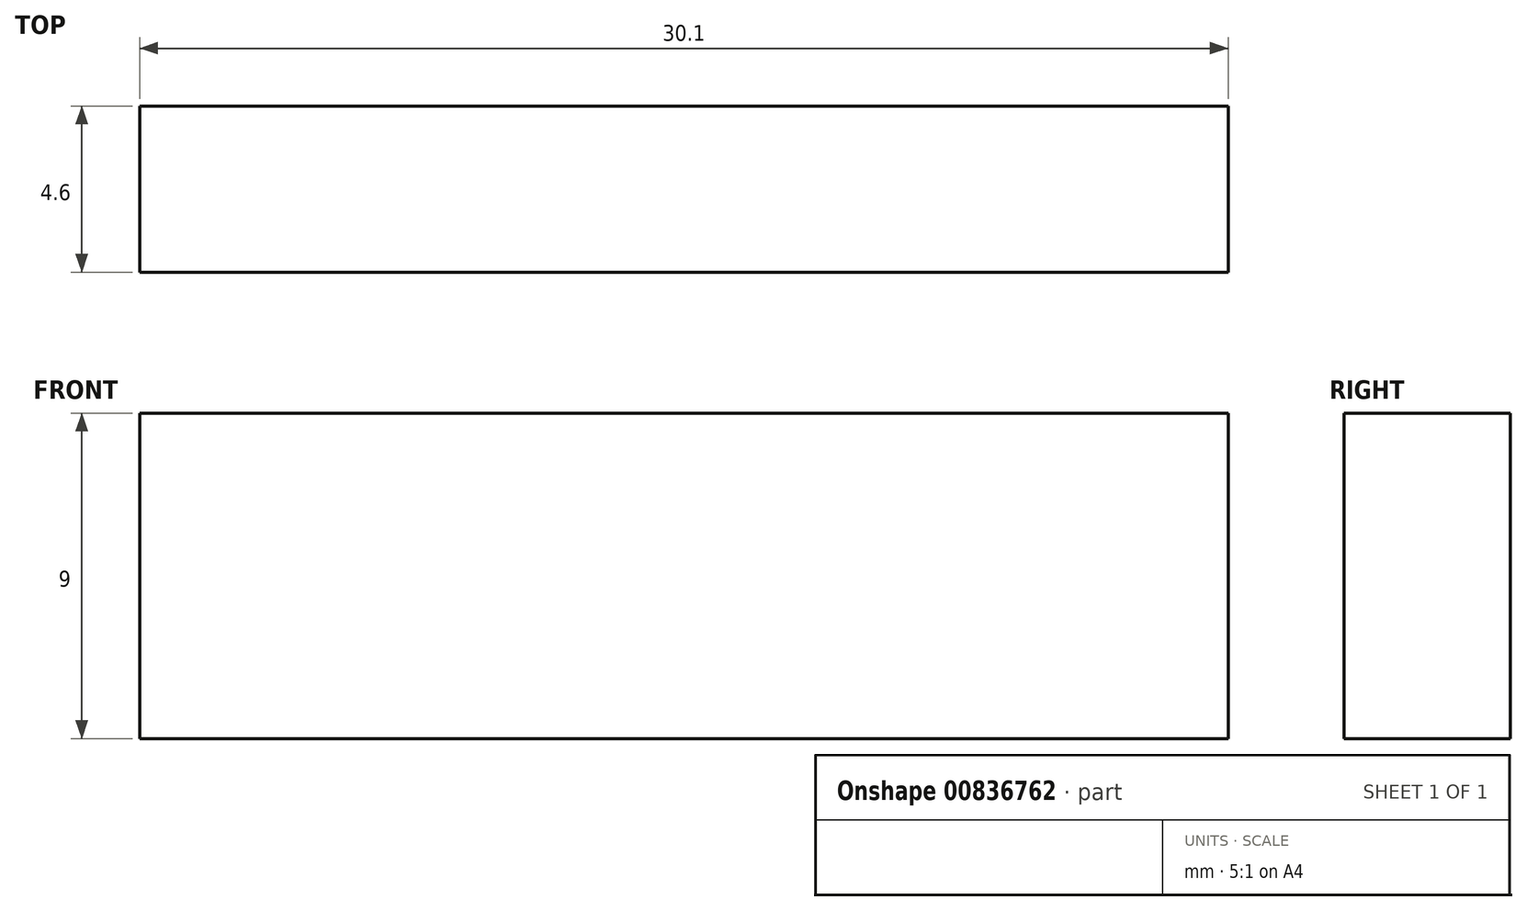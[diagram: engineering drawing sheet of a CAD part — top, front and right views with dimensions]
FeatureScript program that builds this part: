
annotation { "Feature Type Name" : "Feature", "Feature Type Description" : "" }
export const myFeature = defineFeature(function(context is Context, id is Id, definition is map)
    precondition{}
    {
        {
            var Q0;
            Q0=qCreatedBy(makeId("Top.planeOp"),FACE);
            var sketch = newSketch(context, id + "F0", { "sketchPlane" : qUnion([Q0])});
            skLineSegment(sketch, "E0.bottom", {"start": v(15.05, 2.3) * mm, "end": v(-15.05, 2.3) * mm});
            skLineSegment(sketch, "E0.top", {"start": v(15.05, -2.3) * mm, "end": v(-15.05, -2.3) * mm});
            skLineSegment(sketch, "E0.left", {"start": v(15.05, 2.3) * mm, "end": v(15.05, -2.3) * mm});
            skLineSegment(sketch, "E0.right", {"start": v(-15.05, 2.3) * mm, "end": v(-15.05, -2.3) * mm});
            skPoint(sketch, "E0.middle", {"position": v(0, 0) * mm});
            skSolve(sketch);
        }
        {
            var Q0;
            Q0=makeQuery(id+"F0.imprint","IMPRINT",FACE,{"disambiguationData":[TD([[makeQuery(id+"F0.imprint","IMPRINT",EDGE,{"derivedFrom":sQuery(id+"F0.wireOp",EDGE,"E0.bottom")}),1.0]])]});
            extrude(context, id + "F1", {"entities" : qUnion([Q0]), "depth" : 9 * mm, "offsetDistance" : 25 * mm});
        }
    });
